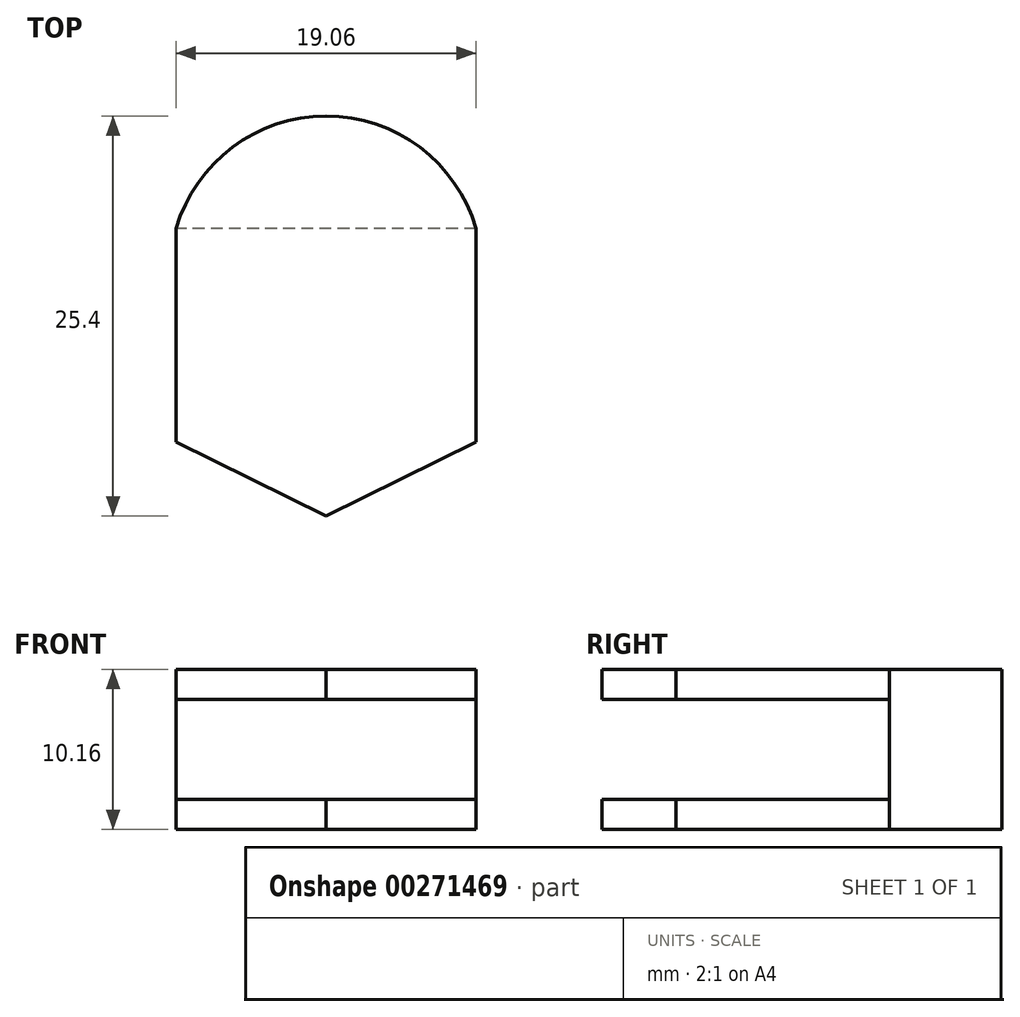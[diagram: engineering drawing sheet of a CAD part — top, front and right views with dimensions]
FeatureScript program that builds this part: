
annotation { "Feature Type Name" : "Feature", "Feature Type Description" : "" }
export const myFeature = defineFeature(function(context is Context, id is Id, definition is map)
    precondition{}
    {
        {
            var Q0;
            Q0=qCreatedBy(makeId("Top.planeOp"),FACE);
            var sketch = newSketch(context, id + "F0", { "sketchPlane" : qUnion([Q0])});
            skLineSegment(sketch, "E0.left", {"start": v(-9.52, 5.56) * mm, "end": v(-9.53, -8.01) * mm});
            skLineSegment(sketch, "E0.right", {"start": v(9.53, 5.56) * mm, "end": v(9.52, -8.01) * mm});
            skPoint(sketch, "E0.middle", {"position": v(0, 0) * mm});
            skLineSegment(sketch, "E1", {"start": v(0, -12.7) * mm, "end": v(-9.53, -8.01) * mm});
            skLineSegment(sketch, "E2", {"start": v(0, -12.7) * mm, "end": v(9.52, -8.01) * mm});
            skArc(sketch, "E3.trimOffspring", {"start": v(9.53, 5.56) * mm, "mid": v(0, 12.7) * mm, "end": v(-9.53, 5.56) * mm});
            skSolve(sketch);
        }
        {
            var Q0;
            Q0 = qSketchRegion(id + "F0", true);
            extrude(context, id + "F1", {"entities" : qUnion([Q0]), "depth" : 10.16 * mm});
        }
        {
            var Q0;
            Q0=makeQuery(id+"F1.opExtrude","SWEPT_FACE",FACE,{"disambiguationData":[OSD([sQuery(id+"F0.wireOp",EDGE,"E0.left")])]});
            var sketch = newSketch(context, id + "F2", { "sketchPlane" : qUnion([Q0])});
            skLineSegment(sketch, "E4.bottom", {"start": v(-5.56, 8.26) * mm, "end": v(21.58, 8.26) * mm});
            skLineSegment(sketch, "E4.top", {"start": v(-5.56, 1.9) * mm, "end": v(21.58, 1.9) * mm});
            skLineSegment(sketch, "E4.left", {"start": v(-5.56, 8.26) * mm, "end": v(-5.56, 1.9) * mm});
            skLineSegment(sketch, "E4.right", {"start": v(21.58, 8.26) * mm, "end": v(21.58, 1.9) * mm});
            skPoint(sketch, "E4.middle", {"position": v(8.01, 5.08) * mm});
            skSolve(sketch);
        }
        {
            var Q0;
            {var subQ0=sQuery(id+"F2.wireOp",EDGE,"E4.right");Q0=makeQuery(id+"F2.imprint","IMPRINT",FACE,{"disambiguationData":[TD([[makeQuery(id+"F2.imprint","IMPRINT",EDGE,{"derivedFrom":subQ0}),-1.0]])]});}
            var Q1;
            {var subQ0=sQuery(id+"F2.wireOp",EDGE,"E4.left");Q1=makeQuery(id+"F2.imprint","IMPRINT",FACE,{"disambiguationData":[TD([[makeQuery(id+"F2.imprint","IMPRINT",EDGE,{"derivedFrom":subQ0}),1.0]])]});}
            extrude(context, id + "F3", {"entities" : qUnion([Q0, Q1]), "operationType" : NewBodyOperationType.REMOVE, "oppositeDirection" : true, "depth" : 25.4 * mm});
        }
    });
